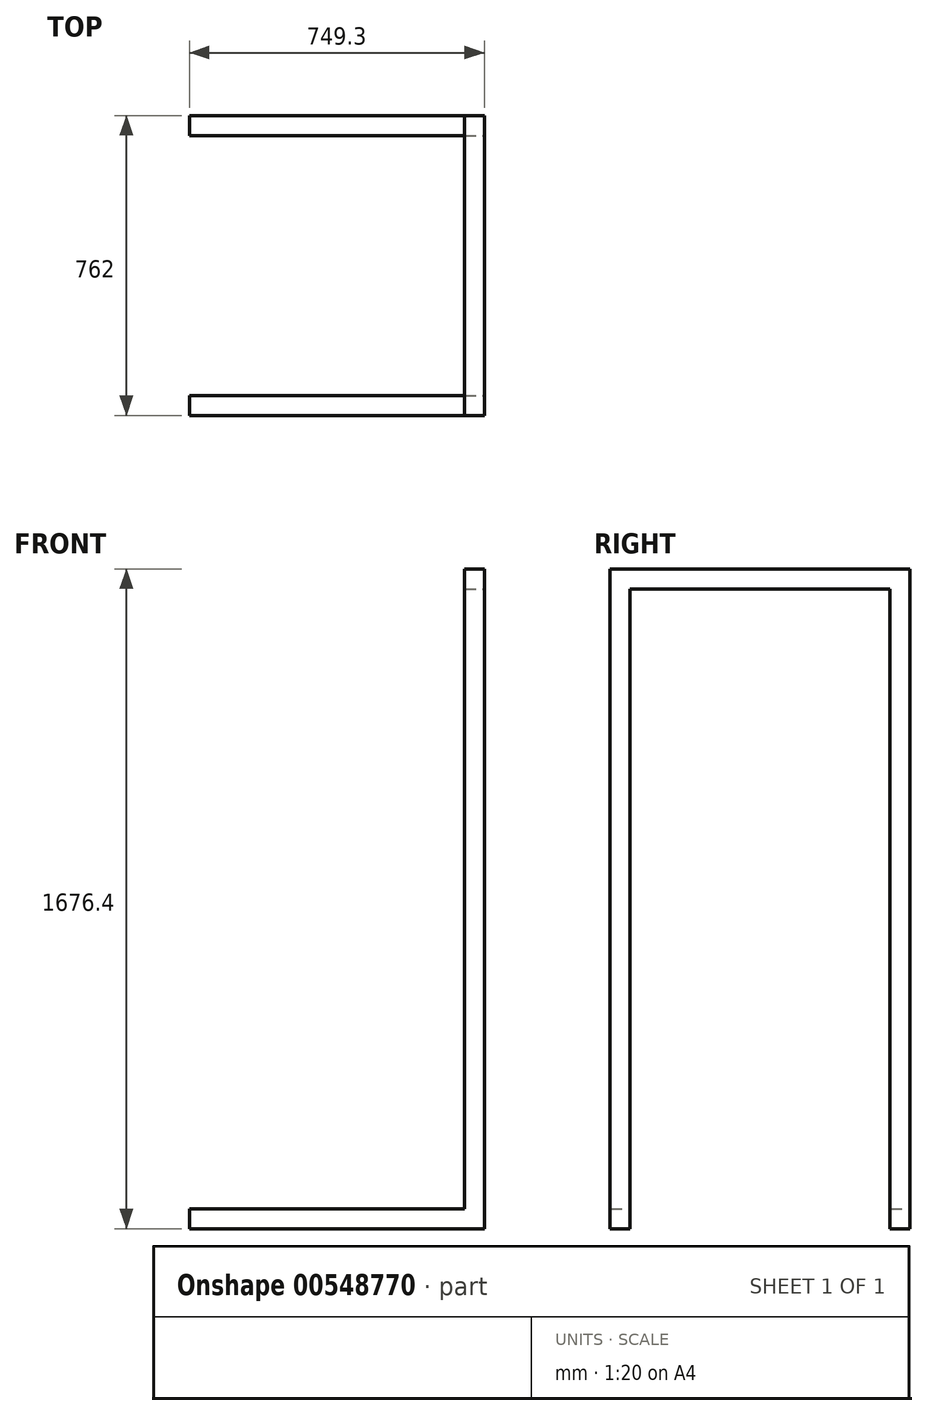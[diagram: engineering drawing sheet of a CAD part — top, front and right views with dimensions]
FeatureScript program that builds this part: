
annotation { "Feature Type Name" : "Feature", "Feature Type Description" : "" }
export const myFeature = defineFeature(function(context is Context, id is Id, definition is map)
    precondition{}
    {
        {
            var Q0;
            Q0=qCreatedBy(makeId("Front.planeOp"),FACE);
            var sketch = newSketch(context, id + "F0", { "sketchPlane" : qUnion([Q0])});
            skLineSegment(sketch, "E0", {"start": v(0, 0) * mm, "end": v(749.3, 0) * mm});
            skLineSegment(sketch, "E1", {"start": v(749.3, 0) * mm, "end": v(749.3, 1676.4) * mm});
            skLineSegment(sketch, "E2", {"start": v(749.3, 1676.4) * mm, "end": v(698.5, 1676.4) * mm});
            skLineSegment(sketch, "E3", {"start": v(698.5, 1676.4) * mm, "end": v(698.5, 50.8) * mm});
            skLineSegment(sketch, "E4", {"start": v(698.5, 50.8) * mm, "end": v(0, 50.8) * mm});
            skLineSegment(sketch, "E5", {"start": v(0, 50.8) * mm, "end": v(0, 0) * mm});
            skSolve(sketch);
        }
        {
            var Q0;
            Q0 = qSketchRegion(id + "F0", true);
            extrude(context, id + "F1", {"entities" : qUnion([Q0]), "depth" : 762 * mm, "offsetDistance" : 25.4 * mm});
        }
        {
            var Q0;
            Q0=makeQuery(id+"F1.opExtrude","SWEPT_FACE",FACE,{"disambiguationData":[OSD([sQuery(id+"F0.wireOp",EDGE,"E1")])]});
            var sketch = newSketch(context, id + "F2", { "sketchPlane" : qUnion([Q0])});
            skLineSegment(sketch, "E6.bottom", {"start": v(-711.2, 0) * mm, "end": v(-50.8, 0) * mm});
            skLineSegment(sketch, "E6.top", {"start": v(-711.2, 1625.6) * mm, "end": v(-50.8, 1625.6) * mm});
            skLineSegment(sketch, "E6.left", {"start": v(-711.2, 0) * mm, "end": v(-711.2, 1625.6) * mm});
            skLineSegment(sketch, "E6.right", {"start": v(-50.8, 0) * mm, "end": v(-50.8, 1625.6) * mm});
            skSolve(sketch);
        }
        {
            var Q0;
            Q0 = qSketchRegion(id + "F2", true);
            extrude(context, id + "F3", {"entities" : qUnion([Q0]), "operationType" : NewBodyOperationType.REMOVE, "endBound" : BoundingType.THROUGH_ALL, "oppositeDirection" : true, "depth" : 25.4 * mm, "offsetDistance" : 25.4 * mm});
        }
    });
